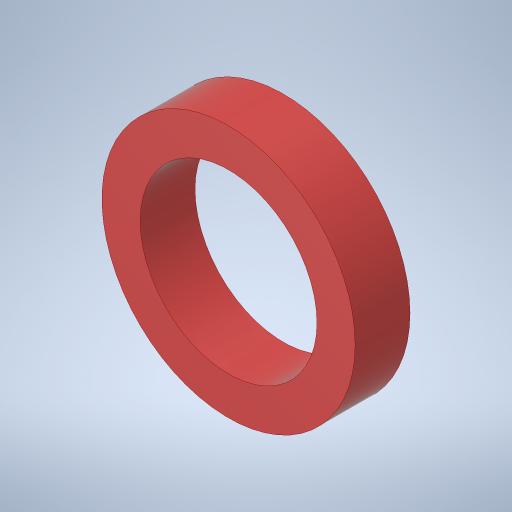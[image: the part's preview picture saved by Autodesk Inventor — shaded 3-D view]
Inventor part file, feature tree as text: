
AUTODESK INVENTOR PART (.ipt)
format: ipt  version: 2023.4 (Build 274418000, 418)  size: 243,712 bytes
history: native  units: in
note: dims shown in document units (in); Inventor stores cm internally (conversion verified against a paired STEP export)
features: extrude x1
ambient origin geometry x8: Origin, YZ Plane, XZ Plane, XY Plane, X Axis, Y Axis, Z Axis, Center Point
bodies: Solid1 (feature_tree)
feature tree (1):
  extrude  "Extrusion1"  TaperAngle=0.0deg  [1 undecoded]
note: 1 required parameter value undecoded (feature->parameter linkage not recoverable at this tier; creation-order binding heuristic only, values carry confidence <= 0.55)
